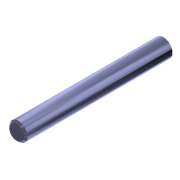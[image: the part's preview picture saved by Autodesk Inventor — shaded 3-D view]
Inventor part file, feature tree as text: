
AUTODESK INVENTOR PART (.ipt)
format: ipt  version: 2015 (Build 190159000, 159)  size: 110,592 bytes
history: native  units: mm
features: extrude x1, chamfer x1, hole x1, sketch x1
ambient origin geometry x8: Origin, YZ Plane, XZ Plane, XY Plane, X Axis, Y Axis, Z Axis, Center Point
bodies: Solid1 (feature_tree)
feature tree (4):
  extrude  "Extrusion1"  Depth=80.0mm TaperAngle=0.0deg
  chamfer  "Chamfer1"  Distance=1.0mm Angle=45.0deg
  hole  "Hole3"  [1 undecoded]
  sketch  "Sketch1"  dims[d0=10.0mm d6=80.0mm d7=0.0mm d48=1.0mm d49=2.0mm d50=45.0deg d51=10.0mm d52=10.0mm d53=4.917mm d54=12.0mm d55=4.0mm d56=2.0mm d57=90.0deg d58=17.1mm d59=20.594885mm]
note: 1 required parameter value undecoded (feature->parameter linkage not recoverable at this tier; creation-order binding heuristic only, values carry confidence <= 0.55)
